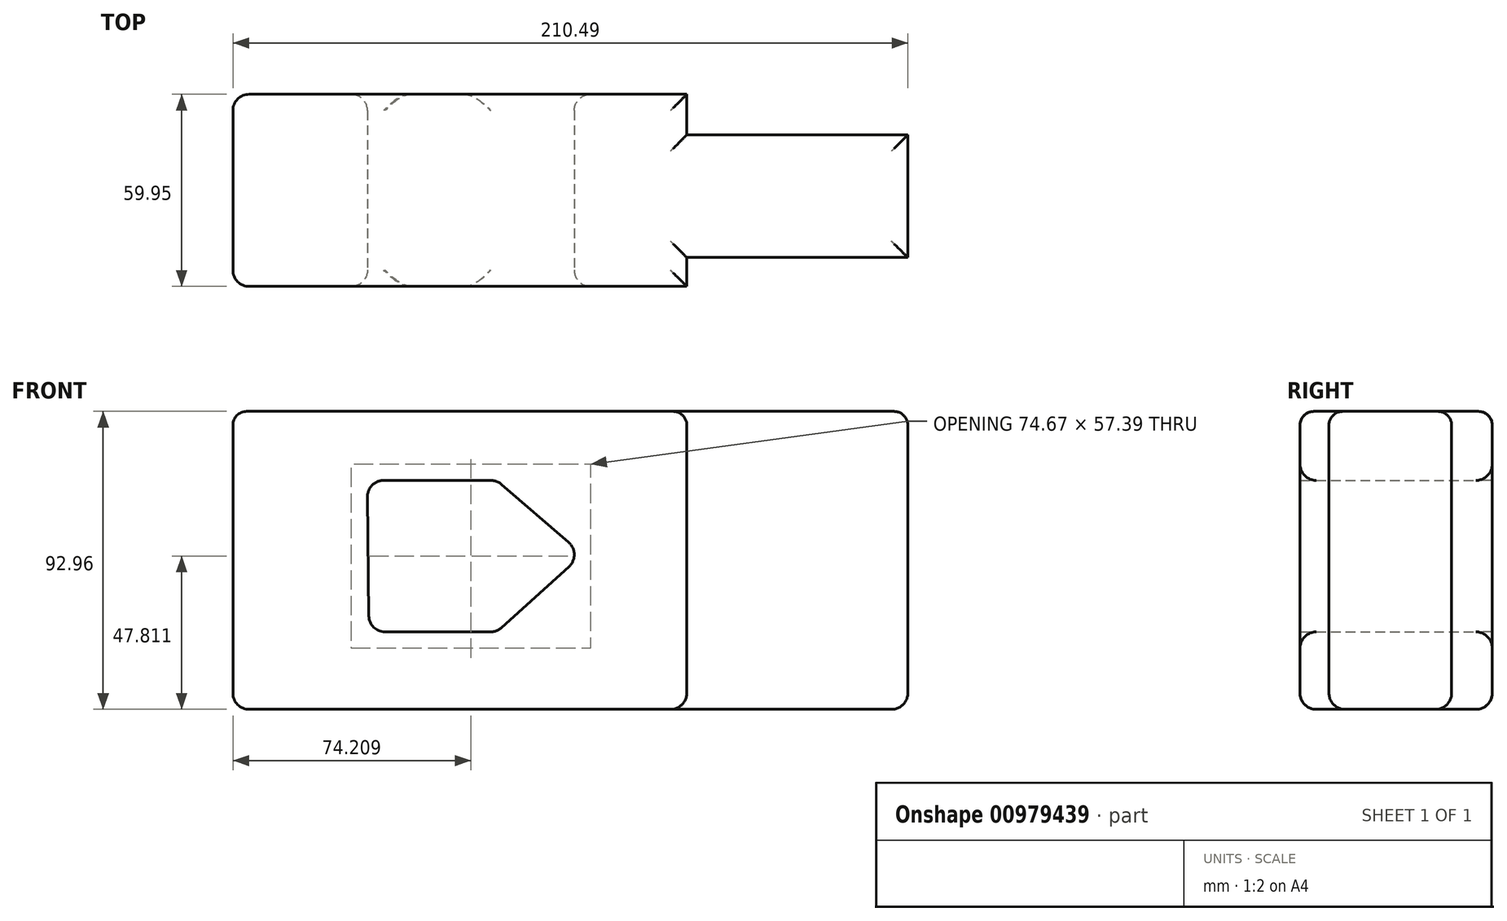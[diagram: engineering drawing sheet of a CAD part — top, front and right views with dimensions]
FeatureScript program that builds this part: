
annotation { "Feature Type Name" : "Feature", "Feature Type Description" : "" }
export const myFeature = defineFeature(function(context is Context, id is Id, definition is map)
    precondition{}
    {
        {
            var Q0;
            Q0=qCreatedBy(makeId("Top.planeOp"),FACE);
            var sketch = newSketch(context, id + "F0", { "sketchPlane" : qUnion([Q0])});
            skLineSegment(sketch, "E0.bottom", {"start": v(-76.89, -11.97) * mm, "end": v(64.67, -11.97) * mm});
            skLineSegment(sketch, "E0.top", {"start": v(-76.89, 47.98) * mm, "end": v(64.67, 47.98) * mm});
            skLineSegment(sketch, "E0.left", {"start": v(-76.89, -11.97) * mm, "end": v(-76.89, 47.98) * mm});
            skLineSegment(sketch, "E0.right", {"start": v(64.67, -11.97) * mm, "end": v(64.67, 47.98) * mm});
            skLineSegment(sketch, "E1.bottom", {"start": v(64.67, 35.32) * mm, "end": v(133.6, 35.32) * mm});
            skLineSegment(sketch, "E1.top", {"start": v(64.67, -2.95) * mm, "end": v(133.6, -2.95) * mm});
            skLineSegment(sketch, "E1.left", {"start": v(64.67, 35.32) * mm, "end": v(64.67, -2.95) * mm});
            skLineSegment(sketch, "E1.right", {"start": v(133.6, 35.32) * mm, "end": v(133.6, -2.95) * mm});
            skSolve(sketch);
        }
        {
            var Q0;
            Q0 = qSketchRegion(id + "F0", true);
            extrude(context, id + "F1", {"entities" : qUnion([Q0]), "depth" : 92.96 * mm, "offsetDistance" : 25.4 * mm});
        }
        {
            var Q0;
            Q0=makeQuery(id+"F1.opExtrude","CAP_FACE",FACE,{"disambiguationData":[OSD([sQuery(id+"F0.wireOp",EDGE,"E0.bottom"),sQuery(id+"F0.wireOp",EDGE,"E0.top"),sQuery(id+"F0.wireOp",EDGE,"E0.left"),sQuery(id+"F0.wireOp",EDGE,"E0.right"),sQuery(id+"F0.wireOp",EDGE,"E1.bottom"),sQuery(id+"F0.wireOp",EDGE,"E1.top"),sQuery(id+"F0.wireOp",EDGE,"E1.right")])],"isStart":false});
            fillet(context, id + "F2", {"entities" : qUnion([Q0]), "radius" : 4.3 * mm, "tangentPropagation" : true, "allowEdgeOverflow" : false});
        }
        {
            var Q0;
            Q0=makeQuery(id+"F1.opExtrude","CAP_EDGE",EDGE,{"disambiguationData":[OSD([sQuery(id+"F0.wireOp",EDGE,"E1.top")])],"isStart":true});
            var Q1;
            Q1=makeQuery(id+"F1.opExtrude","CAP_FACE",FACE,{"disambiguationData":[OSD([sQuery(id+"F0.wireOp",EDGE,"E0.bottom"),sQuery(id+"F0.wireOp",EDGE,"E0.top"),sQuery(id+"F0.wireOp",EDGE,"E0.left"),sQuery(id+"F0.wireOp",EDGE,"E0.right"),sQuery(id+"F0.wireOp",EDGE,"E1.bottom"),sQuery(id+"F0.wireOp",EDGE,"E1.top"),sQuery(id+"F0.wireOp",EDGE,"E1.right")])],"isStart":true});
            fillet(context, id + "F3", {"entities" : qUnion([Q0, Q1]), "radius" : 5.08 * mm, "tangentPropagation" : true, "allowEdgeOverflow" : false});
        }
        {
            var Q0;
            Q0=makeQuery(id+"F1.opExtrude","SWEPT_FACE",FACE,{"disambiguationData":[OSD([sQuery(id+"F0.wireOp",EDGE,"E0.left")])]});
            fillet(context, id + "F4", {"entities" : qUnion([Q0]), "radius" : 5.08 * mm, "tangentPropagation" : true, "allowEdgeOverflow" : false});
        }
        {
            var Q0;
            Q0=makeQuery(id+"F1.opExtrude","SWEPT_FACE",FACE,{"disambiguationData":[OSD([sQuery(id+"F0.wireOp",EDGE,"E0.top")])]});
            var sketch = newSketch(context, id + "F5", { "sketchPlane" : qUnion([Q0])});
            skLineSegment(sketch, "E2", {"start": v(35, 71.44) * mm, "end": v(-5.41, 71.44) * mm});
            skLineSegment(sketch, "E3", {"start": v(-5.41, 71.44) * mm, "end": v(-32.17, 48.36) * mm});
            skLineSegment(sketch, "E4", {"start": v(-32.17, 48.36) * mm, "end": v(-5.41, 24.17) * mm});
            skLineSegment(sketch, "E5", {"start": v(-5.41, 24.17) * mm, "end": v(34.45, 24.17) * mm});
            skLineSegment(sketch, "E6", {"start": v(34.45, 24.17) * mm, "end": v(35, 71.44) * mm});
            skSolve(sketch);
        }
        {
            var Q0;
            Q0=makeQuery(id+"F5.imprint","IMPRINT",FACE,{"disambiguationData":[TD([[makeQuery(id+"F5.imprint","IMPRINT",EDGE,{"derivedFrom":sQuery(id+"F5.wireOp",EDGE,"E2")}),1.0]])]});
            extrude(context, id + "F6", {"entities" : qUnion([Q0]), "operationType" : NewBodyOperationType.REMOVE, "oppositeDirection" : true, "depth" : 66.3 * mm, "offsetDistance" : 25.4 * mm});
        }
        {
            var Q0;
            Q0=makeQuery(id+"F6.boolean.opBoolean","COPY",FACE,{"derivedFrom":makeQuery(id+"F6.opExtrude","SWEPT_FACE",FACE,{"disambiguationData":[OSD([sQuery(id+"F5.wireOp",EDGE,"E6")])]})});
            var Q1;
            Q1=makeQuery(id+"F6.boolean.opBoolean","COPY",FACE,{"derivedFrom":makeQuery(id+"F6.opExtrude","SWEPT_FACE",FACE,{"disambiguationData":[OSD([sQuery(id+"F5.wireOp",EDGE,"E3")])]})});
            var Q2;
            Q2=makeQuery(id+"F6.boolean.opBoolean","COPY",FACE,{"derivedFrom":makeQuery(id+"F6.opExtrude","SWEPT_FACE",FACE,{"disambiguationData":[OSD([sQuery(id+"F5.wireOp",EDGE,"E4")])]})});
            fillet(context, id + "F7", {"entities" : qUnion([Q0, Q1, Q2]), "radius" : 5.08 * mm, "tangentPropagation" : true, "allowEdgeOverflow" : false});
        }
    });
